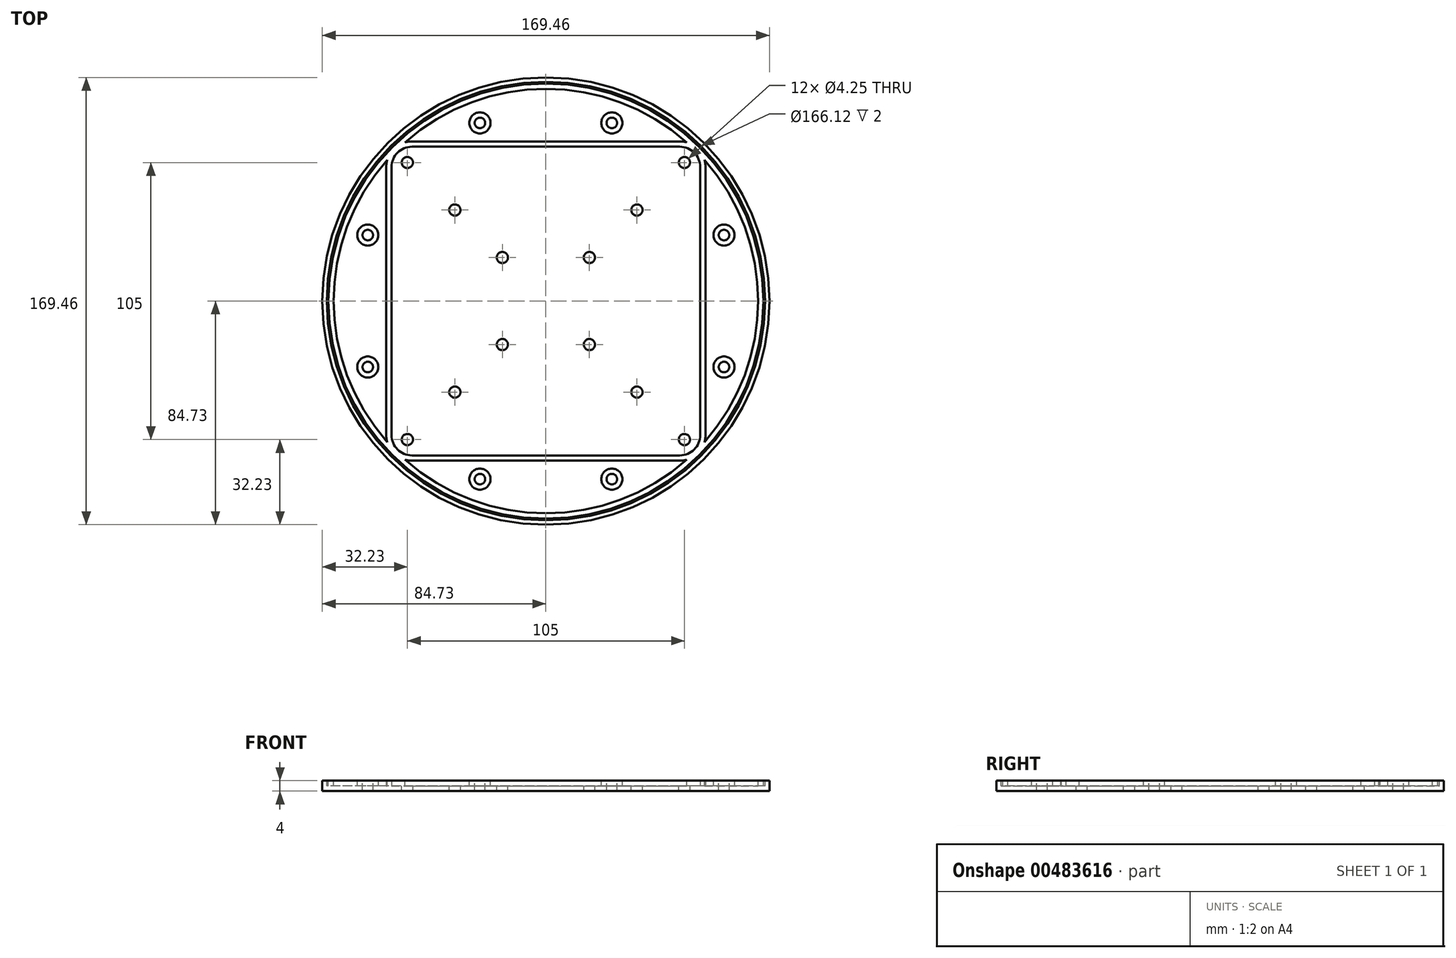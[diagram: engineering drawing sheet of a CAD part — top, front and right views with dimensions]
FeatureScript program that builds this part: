
annotation { "Feature Type Name" : "Feature", "Feature Type Description" : "" }
export const myFeature = defineFeature(function(context is Context, id is Id, definition is map)
    precondition{}
    {
        {
            var Q0;
            Q0=qCreatedBy(makeId("Top.planeOp"),FACE);
            var sketch = newSketch(context, id + "F0", { "sketchPlane" : qUnion([Q0])});
            skLineSegment(sketch, "E0.bottom", {"start": v(50.75, 58.5) * mm, "end": v(-50.75, 58.5) * mm});
            skLineSegment(sketch, "E0.top", {"start": v(50.75, -58.5) * mm, "end": v(-50.75, -58.5) * mm});
            skLineSegment(sketch, "E0.left", {"start": v(58.5, 50.75) * mm, "end": v(58.5, -50.75) * mm});
            skLineSegment(sketch, "E0.right", {"start": v(-58.5, 50.75) * mm, "end": v(-58.5, -50.75) * mm});
            skPoint(sketch, "E0.middle", {"position": v(0, 0) * mm});
            skCircle(sketch, "E1", {"center": v(0, 0) * mm, "radius": 82.73 * mm});
            skCircle(sketch, "E2", {"center": v(0, 0) * mm, "radius": 84.73 * mm});
            skLineSegment(sketch, "E3.bottom", {"start": v(48.75, 56.5) * mm, "end": v(-48.75, 56.5) * mm});
            skLineSegment(sketch, "E3.top", {"start": v(48.75, -56.5) * mm, "end": v(-48.75, -56.5) * mm});
            skLineSegment(sketch, "E3.left", {"start": v(56.5, 48.75) * mm, "end": v(56.5, -48.75) * mm});
            skLineSegment(sketch, "E3.right", {"start": v(-56.5, 48.75) * mm, "end": v(-56.5, -48.75) * mm});
            skLineSegment(sketch, "E4", {"start": v(-24, 58.5) * mm, "end": v(-24, 56.5) * mm});
            skLineSegment(sketch, "E5.MirrorCS", {"start": v(24, 58.5) * mm, "end": v(24, 56.5) * mm});
            skLineSegment(sketch, "E6.1.0", {"start": v(-58.5, -24) * mm, "end": v(-56.5, -24) * mm});
            skLineSegment(sketch, "E6.1.1", {"start": v(-58.5, 24) * mm, "end": v(-56.5, 24) * mm});
            skLineSegment(sketch, "E6.2.0", {"start": v(24, -58.5) * mm, "end": v(24, -56.5) * mm});
            skLineSegment(sketch, "E6.2.1", {"start": v(-24, -58.5) * mm, "end": v(-24, -56.5) * mm});
            skLineSegment(sketch, "E6.3.0", {"start": v(58.5, 24) * mm, "end": v(56.5, 24) * mm});
            skLineSegment(sketch, "E6.3.1", {"start": v(58.5, -24) * mm, "end": v(56.5, -24) * mm});
            skPoint(sketch, "E7.visualSharp", {"position": v(-58.5, 58.5) * mm});
            skArc(sketch, "E7.filletArc", {"start": v(-50.75, 58.5) * mm, "mid": v(-56.23, 56.23) * mm, "end": v(-58.5, 50.75) * mm});
            skPoint(sketch, "E8.visualSharp", {"position": v(-56.5, 56.5) * mm});
            skArc(sketch, "E8.filletArc", {"start": v(-48.75, 56.5) * mm, "mid": v(-54.23, 54.23) * mm, "end": v(-56.5, 48.75) * mm});
            skPoint(sketch, "E9.visualSharp", {"position": v(56.5, 56.5) * mm});
            skArc(sketch, "E9.filletArc", {"start": v(56.5, 48.75) * mm, "mid": v(54.23, 54.23) * mm, "end": v(48.75, 56.5) * mm});
            skPoint(sketch, "E10.visualSharp", {"position": v(58.5, 58.5) * mm});
            skArc(sketch, "E10.filletArc", {"start": v(58.5, 50.75) * mm, "mid": v(56.23, 56.23) * mm, "end": v(50.75, 58.5) * mm});
            skPoint(sketch, "E11.visualSharp", {"position": v(56.5, -56.5) * mm});
            skArc(sketch, "E11.filletArc", {"start": v(48.75, -56.5) * mm, "mid": v(54.23, -54.23) * mm, "end": v(56.5, -48.75) * mm});
            skPoint(sketch, "E12.visualSharp", {"position": v(58.5, -58.5) * mm});
            skArc(sketch, "E12.filletArc", {"start": v(50.75, -58.5) * mm, "mid": v(56.23, -56.23) * mm, "end": v(58.5, -50.75) * mm});
            skPoint(sketch, "E13.visualSharp", {"position": v(-58.5, -58.5) * mm});
            skArc(sketch, "E13.filletArc", {"start": v(-58.5, -50.75) * mm, "mid": v(-56.23, -56.23) * mm, "end": v(-50.75, -58.5) * mm});
            skPoint(sketch, "E14.visualSharp", {"position": v(-56.5, -56.5) * mm});
            skArc(sketch, "E14.filletArc", {"start": v(-56.5, -48.75) * mm, "mid": v(-54.23, -54.23) * mm, "end": v(-48.75, -56.5) * mm});
            skSolve(sketch);
        }
        {
            var Q0;
            {var subQ3=sQuery(id+"F0.wireOp",EDGE,"E6.1.0");Q0=makeQuery(id+"F0.imprint","IMPRINT",FACE,{"disambiguationData":[TD([[makeQuery(id+"F0.imprint","IMPRINT",EDGE,{"derivedFrom":subQ3}),-1.0]])]});}
            var Q1;
            {var subQ7=sQuery(id+"F0.wireOp",EDGE,"E6.2.0");Q1=makeQuery(id+"F0.imprint","IMPRINT",FACE,{"disambiguationData":[TD([[makeQuery(id+"F0.imprint","IMPRINT",EDGE,{"derivedFrom":subQ7}),-1.0]])]});}
            var Q2;
            {var subQ4=sQuery(id+"F0.wireOp",EDGE,"E5.MirrorCS");Q2=makeQuery(id+"F0.imprint","IMPRINT",FACE,{"disambiguationData":[TD([[makeQuery(id+"F0.imprint","IMPRINT",EDGE,{"derivedFrom":subQ4}),1.0]])]});}
            var Q3;
            {var subQ4=sQuery(id+"F0.wireOp",EDGE,"E4");Q3=makeQuery(id+"F0.imprint","IMPRINT",FACE,{"disambiguationData":[TD([[makeQuery(id+"F0.imprint","IMPRINT",EDGE,{"derivedFrom":subQ4}),-1.0]])]});}
            var Q4;
            {var subQ1=sQuery(id+"F0.wireOp",EDGE,"E0.top");var subQ3=makeQuery(id+"F0.imprint","INTERSECT",VERTEX,{"derivedFrom":[subQ1,sQuery(id+"F0.wireOp",EDGE,"E6.2.0")]});Q4=makeQuery(id+"F0.imprint","IMPRINT",FACE,{"disambiguationData":[TD([[makeQuery(id+"F0.imprint","IMPRINT",EDGE,{"disambiguationData":[TD([[subQ3,-1.0]])],"derivedFrom":subQ1}),1.0]])]});}
            var Q5;
            {var subQ1=sQuery(id+"F0.wireOp",EDGE,"E0.right");var subQ4=makeQuery(id+"F0.imprint","INTERSECT",VERTEX,{"derivedFrom":[subQ1,sQuery(id+"F0.wireOp",EDGE,"E6.1.0")]});Q5=makeQuery(id+"F0.imprint","IMPRINT",FACE,{"disambiguationData":[TD([[makeQuery(id+"F0.imprint","IMPRINT",EDGE,{"disambiguationData":[TD([[subQ4,1.0]])],"derivedFrom":subQ1}),-1.0]])]});}
            var Q6;
            {var subQ1=sQuery(id+"F0.wireOp",EDGE,"E0.bottom");var subQ4=makeQuery(id+"F0.imprint","INTERSECT",VERTEX,{"derivedFrom":[subQ1,sQuery(id+"F0.wireOp",EDGE,"E4")]});Q6=makeQuery(id+"F0.imprint","IMPRINT",FACE,{"disambiguationData":[TD([[makeQuery(id+"F0.imprint","IMPRINT",EDGE,{"disambiguationData":[TD([[subQ4,1.0]])],"derivedFrom":subQ1}),-1.0]])]});}
            var Q7;
            {var subQ1=sQuery(id+"F0.wireOp",EDGE,"E0.left");var subQ3=makeQuery(id+"F0.imprint","INTERSECT",VERTEX,{"derivedFrom":[subQ1,sQuery(id+"F0.wireOp",EDGE,"E6.3.0")]});Q7=makeQuery(id+"F0.imprint","IMPRINT",FACE,{"disambiguationData":[TD([[makeQuery(id+"F0.imprint","IMPRINT",EDGE,{"disambiguationData":[TD([[subQ3,-1.0]])],"derivedFrom":subQ1}),1.0]])]});}
            var Q8;
            Q8=makeQuery(id+"F0.imprint","IMPRINT",FACE,{"disambiguationData":[TD([[makeQuery(id+"F0.imprint","IMPRINT",EDGE,{"derivedFrom":sQuery(id+"F0.wireOp",EDGE,"E2")}),1.0]])]});
            var Q9;
            {var subQ1=sQuery(id+"F0.wireOp",EDGE,"E3.bottom");var subQ4=sQuery(id+"F0.wireOp",EDGE,"E3.left");var subQ9=makeQuery(id+"F0.imprint","INTERSECT",VERTEX,{"derivedFrom":[subQ1,subQ4]});Q9=makeQuery(id+"F0.imprint","IMPRINT",FACE,{"disambiguationData":[TD([[makeQuery(id+"F0.imprint","IMPRINT",EDGE,{"disambiguationData":[TD([[subQ9,-1.0]])],"derivedFrom":subQ1}),1.0]])]});}
            var Q10;
            {var subQ0=sQuery(id+"F0.wireOp",EDGE,"E6.1.0");Q10=makeQuery(id+"F0.imprint","IMPRINT",FACE,{"disambiguationData":[TD([[makeQuery(id+"F0.imprint","IMPRINT",EDGE,{"derivedFrom":subQ0}),1.0]])]});}
            var Q11;
            {var subQ0=sQuery(id+"F0.wireOp",EDGE,"E4");Q11=makeQuery(id+"F0.imprint","IMPRINT",FACE,{"disambiguationData":[TD([[makeQuery(id+"F0.imprint","IMPRINT",EDGE,{"derivedFrom":subQ0}),1.0]])]});}
            var Q12;
            {var subQ0=sQuery(id+"F0.wireOp",EDGE,"E6.2.0");Q12=makeQuery(id+"F0.imprint","IMPRINT",FACE,{"disambiguationData":[TD([[makeQuery(id+"F0.imprint","IMPRINT",EDGE,{"derivedFrom":subQ0}),1.0]])]});}
            var Q13;
            {var subQ0=sQuery(id+"F0.wireOp",EDGE,"E6.3.0");Q13=makeQuery(id+"F0.imprint","IMPRINT",FACE,{"disambiguationData":[TD([[makeQuery(id+"F0.imprint","IMPRINT",EDGE,{"derivedFrom":subQ0}),1.0]])]});}
            extrude(context, id + "F1", {"entities" : qUnion([Q0, Q1, Q2, Q3, Q4, Q5, Q6, Q7, Q8, Q9, Q10, Q11, Q12, Q13]), "depth" : 2 * mm});
        }
        {
            var Q0;
            {var subQ1=sQuery(id+"F0.wireOp",EDGE,"E0.top");var subQ3=makeQuery(id+"F0.imprint","INTERSECT",VERTEX,{"derivedFrom":[subQ1,sQuery(id+"F0.wireOp",EDGE,"E6.2.0")]});Q0=makeQuery(id+"F0.imprint","IMPRINT",FACE,{"disambiguationData":[TD([[makeQuery(id+"F0.imprint","IMPRINT",EDGE,{"disambiguationData":[TD([[subQ3,-1.0]])],"derivedFrom":subQ1}),1.0]])]});}
            var Q1;
            {var subQ1=sQuery(id+"F0.wireOp",EDGE,"E0.right");var subQ4=makeQuery(id+"F0.imprint","INTERSECT",VERTEX,{"derivedFrom":[subQ1,sQuery(id+"F0.wireOp",EDGE,"E6.1.0")]});Q1=makeQuery(id+"F0.imprint","IMPRINT",FACE,{"disambiguationData":[TD([[makeQuery(id+"F0.imprint","IMPRINT",EDGE,{"disambiguationData":[TD([[subQ4,1.0]])],"derivedFrom":subQ1}),-1.0]])]});}
            var Q2;
            Q2=makeQuery(id+"F0.imprint","IMPRINT",FACE,{"disambiguationData":[TD([[makeQuery(id+"F0.imprint","IMPRINT",EDGE,{"derivedFrom":sQuery(id+"F0.wireOp",EDGE,"E2")}),1.0]])]});
            var Q3;
            {var subQ1=sQuery(id+"F0.wireOp",EDGE,"E0.bottom");var subQ4=makeQuery(id+"F0.imprint","INTERSECT",VERTEX,{"derivedFrom":[subQ1,sQuery(id+"F0.wireOp",EDGE,"E4")]});Q3=makeQuery(id+"F0.imprint","IMPRINT",FACE,{"disambiguationData":[TD([[makeQuery(id+"F0.imprint","IMPRINT",EDGE,{"disambiguationData":[TD([[subQ4,1.0]])],"derivedFrom":subQ1}),-1.0]])]});}
            var Q4;
            {var subQ1=sQuery(id+"F0.wireOp",EDGE,"E0.left");var subQ3=makeQuery(id+"F0.imprint","INTERSECT",VERTEX,{"derivedFrom":[subQ1,sQuery(id+"F0.wireOp",EDGE,"E6.3.0")]});Q4=makeQuery(id+"F0.imprint","IMPRINT",FACE,{"disambiguationData":[TD([[makeQuery(id+"F0.imprint","IMPRINT",EDGE,{"disambiguationData":[TD([[subQ3,-1.0]])],"derivedFrom":subQ1}),1.0]])]});}
            extrude(context, id + "F2", {"entities" : qUnion([Q0, Q1, Q2, Q3, Q4]), "operationType" : NewBodyOperationType.ADD, "depth" : 4 * mm});
        }
        {
            var Q0;
            Q0=makeQuery(id+"F2.opExtrude","CAP_FACE",FACE,{"disambiguationData":[OSD([sQuery(id+"F0.wireOp",EDGE,"E0.bottom"),sQuery(id+"F0.wireOp",EDGE,"E0.top"),sQuery(id+"F0.wireOp",EDGE,"E0.left"),sQuery(id+"F0.wireOp",EDGE,"E0.right"),sQuery(id+"F0.wireOp",EDGE,"E2")])],"isStart":false});
            var sketch = newSketch(context, id + "F3", { "sketchPlane" : qUnion([Q0])});
            skCircle(sketch, "E15", {"center": v(0, 0) * mm, "radius": 82.44 * mm});
            skCircle(sketch, "E16", {"center": v(0, 0) * mm, "radius": 83.06 * mm});
            skSolve(sketch);
        }
        {
            var Q0;
            Q0=makeQuery(id+"F3.imprint","IMPRINT",FACE,{"disambiguationData":[TD([[makeQuery(id+"F3.imprint","IMPRINT",EDGE,{"derivedFrom":sQuery(id+"F3.wireOp",EDGE,"E15")}),-1.0]])]});
            extrude(context, id + "F4", {"entities" : qUnion([Q0]), "operationType" : NewBodyOperationType.REMOVE, "oppositeDirection" : true, "depth" : 2 * mm});
        }
        {
            var Q0;
            Q0=makeQuery(id+"F1.opExtrude","CAP_FACE",FACE,{"disambiguationData":[OSD([sQuery(id+"F0.wireOp",EDGE,"E2")])],"isStart":false});
            var sketch = newSketch(context, id + "F5", { "sketchPlane" : qUnion([Q0])});
            skPoint(sketch, "E17.middle", {"position": v(0, 0) * mm});
            skLineSegment(sketch, "E18.bottom", {"start": v(58.5, 58.5) * mm, "end": v(-58.5, 58.5) * mm});
            skLineSegment(sketch, "E18.top", {"start": v(58.5, -58.5) * mm, "end": v(-58.5, -58.5) * mm});
            skLineSegment(sketch, "E18.left", {"start": v(58.5, 58.5) * mm, "end": v(58.5, -58.5) * mm});
            skLineSegment(sketch, "E18.right", {"start": v(-58.5, 58.5) * mm, "end": v(-58.5, -58.5) * mm});
            skCircle(sketch, "E19", {"center": v(-52.5, 52.5) * mm, "radius": 2.12 * mm});
            skCircle(sketch, "E20.1.0", {"center": v(-52.5, -52.5) * mm, "radius": 2.12 * mm});
            skCircle(sketch, "E20.2.0", {"center": v(52.5, -52.5) * mm, "radius": 2.12 * mm});
            skCircle(sketch, "E20.3.0", {"center": v(52.5, 52.5) * mm, "radius": 2.12 * mm});
            skCircle(sketch, "E21", {"center": v(-16.5, 16.5) * mm, "radius": 2.12 * mm});
            skCircle(sketch, "E22.1.0", {"center": v(-16.5, -16.5) * mm, "radius": 2.12 * mm});
            skCircle(sketch, "E22.2.0", {"center": v(16.5, -16.5) * mm, "radius": 2.12 * mm});
            skCircle(sketch, "E22.3.0", {"center": v(16.5, 16.5) * mm, "radius": 2.12 * mm});
            skCircle(sketch, "E23", {"center": v(34.5, -34.5) * mm, "radius": 2.12 * mm});
            skCircle(sketch, "E24.1.0", {"center": v(34.5, 34.5) * mm, "radius": 2.12 * mm});
            skCircle(sketch, "E24.2.0", {"center": v(-34.5, 34.5) * mm, "radius": 2.12 * mm});
            skCircle(sketch, "E24.3.0", {"center": v(-34.5, -34.5) * mm, "radius": 2.12 * mm});
            skSolve(sketch);
        }
        {
            var Q0;
            Q0=makeQuery(id+"F5.imprint","IMPRINT",FACE,{"disambiguationData":[TD([[makeQuery(id+"F5.imprint","IMPRINT",EDGE,{"derivedFrom":sQuery(id+"F5.wireOp",EDGE,"E19")}),1.0]])]});
            var Q1;
            Q1=makeQuery(id+"F5.imprint","IMPRINT",FACE,{"disambiguationData":[TD([[makeQuery(id+"F5.imprint","IMPRINT",EDGE,{"derivedFrom":sQuery(id+"F5.wireOp",EDGE,"E20.3.0")}),1.0]])]});
            var Q2;
            Q2=makeQuery(id+"F5.imprint","IMPRINT",FACE,{"disambiguationData":[TD([[makeQuery(id+"F5.imprint","IMPRINT",EDGE,{"derivedFrom":sQuery(id+"F5.wireOp",EDGE,"E20.1.0")}),1.0]])]});
            var Q3;
            Q3=makeQuery(id+"F5.imprint","IMPRINT",FACE,{"disambiguationData":[TD([[makeQuery(id+"F5.imprint","IMPRINT",EDGE,{"derivedFrom":sQuery(id+"F5.wireOp",EDGE,"E20.2.0")}),1.0]])]});
            var Q4;
            Q4=makeQuery(id+"F5.imprint","IMPRINT",FACE,{"disambiguationData":[TD([[makeQuery(id+"F5.imprint","IMPRINT",EDGE,{"derivedFrom":sQuery(id+"F5.wireOp",EDGE,"E22.3.0")}),1.0]])]});
            var Q5;
            Q5=makeQuery(id+"F5.imprint","IMPRINT",FACE,{"disambiguationData":[TD([[makeQuery(id+"F5.imprint","IMPRINT",EDGE,{"derivedFrom":sQuery(id+"F5.wireOp",EDGE,"E21")}),1.0]])]});
            var Q6;
            Q6=makeQuery(id+"F5.imprint","IMPRINT",FACE,{"disambiguationData":[TD([[makeQuery(id+"F5.imprint","IMPRINT",EDGE,{"derivedFrom":sQuery(id+"F5.wireOp",EDGE,"E22.1.0")}),1.0]])]});
            var Q7;
            Q7=makeQuery(id+"F5.imprint","IMPRINT",FACE,{"disambiguationData":[TD([[makeQuery(id+"F5.imprint","IMPRINT",EDGE,{"derivedFrom":sQuery(id+"F5.wireOp",EDGE,"E22.2.0")}),1.0]])]});
            var Q8;
            Q8=makeQuery(id+"F5.imprint","IMPRINT",FACE,{"disambiguationData":[TD([[makeQuery(id+"F5.imprint","IMPRINT",EDGE,{"derivedFrom":sQuery(id+"F5.wireOp",EDGE,"E24.2.0")}),1.0]])]});
            var Q9;
            Q9=makeQuery(id+"F5.imprint","IMPRINT",FACE,{"disambiguationData":[TD([[makeQuery(id+"F5.imprint","IMPRINT",EDGE,{"derivedFrom":sQuery(id+"F5.wireOp",EDGE,"E24.1.0")}),1.0]])]});
            var Q10;
            Q10=makeQuery(id+"F5.imprint","IMPRINT",FACE,{"disambiguationData":[TD([[makeQuery(id+"F5.imprint","IMPRINT",EDGE,{"derivedFrom":sQuery(id+"F5.wireOp",EDGE,"E23")}),1.0]])]});
            var Q11;
            Q11=makeQuery(id+"F5.imprint","IMPRINT",FACE,{"disambiguationData":[TD([[makeQuery(id+"F5.imprint","IMPRINT",EDGE,{"derivedFrom":sQuery(id+"F5.wireOp",EDGE,"E24.3.0")}),1.0]])]});
            extrude(context, id + "F6", {"entities" : qUnion([Q0, Q1, Q2, Q3, Q4, Q5, Q6, Q7, Q8, Q9, Q10, Q11]), "operationType" : NewBodyOperationType.REMOVE, "oppositeDirection" : true, "depth" : 25 * mm});
        }
        {
            var Q0;
            Q0=makeQuery(id+"F1.opExtrude","CAP_FACE",FACE,{"disambiguationData":[OSD([sQuery(id+"F0.wireOp",EDGE,"E2")])],"isStart":false});
            var sketch = newSketch(context, id + "F7", { "sketchPlane" : qUnion([Q0])});
            skCircle(sketch, "E25", {"center": v(0, -8) * mm, "radius": 14.5 * mm});
            skCircle(sketch, "E26", {"center": v(-17.5, -8) * mm, "radius": 1.5 * mm});
            skCircle(sketch, "E27.1.0", {"center": v(17.5, -8) * mm, "radius": 1.5 * mm});
            skCircle(sketch, "E28", {"center": v(-17.5, -8) * mm, "radius": 3 * mm});
            skCircle(sketch, "E29.1.0", {"center": v(17.5, -8) * mm, "radius": 3 * mm});
            skSolve(sketch);
        }
        {
            var Q0;
            {var subQ0=sQuery(id+"F0.wireOp",EDGE,"E0.left");var subQ1=sQuery(id+"F0.wireOp",EDGE,"E0.top");var subQ2=sQuery(id+"F0.wireOp",EDGE,"E0.right");var subQ3=sQuery(id+"F0.wireOp",EDGE,"E0.bottom");var subQ4=sQuery(id+"F0.wireOp",EDGE,"E7.filletArc");var subQ5=sQuery(id+"F0.wireOp",EDGE,"E10.filletArc");var subQ6=sQuery(id+"F0.wireOp",EDGE,"E12.filletArc");var subQ7=sQuery(id+"F0.wireOp",EDGE,"E13.filletArc");Q0=makeQuery(id+"F4.boolean.opBoolean","SPLIT",FACE,{"disambiguationData":[TD([makeQuery(id+"F2.opExtrude","SWEPT_FACE",FACE,{"disambiguationData":[OSD([subQ3])]})])],"derivedFrom":makeQuery(id+"F2.opExtrude","CAP_FACE",FACE,{"disambiguationData":[OSD([subQ3,subQ1,subQ0,subQ2,sQuery(id+"F0.wireOp",EDGE,"E2"),subQ4,subQ5,subQ6,subQ7])],"isStart":false})});}
            var sketch = newSketch(context, id + "F8", { "sketchPlane" : qUnion([Q0])});
            skLineSegment(sketch, "E30.bottom", {"start": v(25, 67.5) * mm, "end": v(-25, 67.5) * mm});
            skLineSegment(sketch, "E30.top", {"start": v(25, -67.5) * mm, "end": v(-25, -67.5) * mm});
            skLineSegment(sketch, "E30.left", {"start": v(25, 67.5) * mm, "end": v(25, -67.5) * mm});
            skLineSegment(sketch, "E30.right", {"start": v(-25, 67.5) * mm, "end": v(-25, -67.5) * mm});
            skPoint(sketch, "E30.middle", {"position": v(0, 0) * mm});
            skLineSegment(sketch, "E31.bottom", {"start": v(67.5, 25) * mm, "end": v(-67.5, 25) * mm});
            skLineSegment(sketch, "E31.top", {"start": v(67.5, -25) * mm, "end": v(-67.5, -25) * mm});
            skLineSegment(sketch, "E31.left", {"start": v(67.5, 25) * mm, "end": v(67.5, -25) * mm});
            skLineSegment(sketch, "E31.right", {"start": v(-67.5, 25) * mm, "end": v(-67.5, -25) * mm});
            skSolve(sketch);
        }
        {
            var Q0;
            Q0=sQuery(id+"F8.wireOp",VERTEX,"E30.right.start");
            var Q1;
            Q1=sQuery(id+"F8.wireOp",VERTEX,"E30.left.start");
            var Q2;
            Q2=sQuery(id+"F8.wireOp",VERTEX,"E31.left.start");
            var Q3;
            Q3=sQuery(id+"F8.wireOp",VERTEX,"E31.top.start");
            var Q4;
            Q4=sQuery(id+"F8.wireOp",VERTEX,"E30.left.end");
            var Q5;
            Q5=sQuery(id+"F8.wireOp",VERTEX,"E31.bottom.end");
            var Q6;
            Q6=sQuery(id+"F8.wireOp",VERTEX,"E30.right.end");
            var Q7;
            Q7=sQuery(id+"F8.wireOp",VERTEX,"E31.top.end");
            var Q8;
            Q8=makeQuery(id+"F1.opExtrude","SWEPT_BODY",BODY,{"disambiguationData":[OSD([sQuery(id+"F0.wireOp",EDGE,"E2")])]});
            hole(context, id + "F9", {"style" : HoleStyle.SIMPLE, "endStyle" : HoleEndStyle.BLIND, "holeDiameter" : 4 * mm, "holeDepth" : 12 * mm, "isTappedThrough" : true, "tappedDepth" : 12 * mm, "tapClearance" : 3, "locations" : qUnion([Q0, Q1, Q2, Q3, Q4, Q5, Q6, Q7]), "scope" : qUnion([Q8])});
        }
        {
            var Q0;
            {var subQ0=sQuery(id+"F0.wireOp",EDGE,"E0.left");var subQ1=sQuery(id+"F0.wireOp",EDGE,"E0.top");var subQ2=sQuery(id+"F0.wireOp",EDGE,"E0.right");var subQ3=sQuery(id+"F0.wireOp",EDGE,"E0.bottom");var subQ4=sQuery(id+"F0.wireOp",EDGE,"E7.filletArc");var subQ5=sQuery(id+"F0.wireOp",EDGE,"E10.filletArc");var subQ6=sQuery(id+"F0.wireOp",EDGE,"E12.filletArc");var subQ7=sQuery(id+"F0.wireOp",EDGE,"E13.filletArc");Q0=makeQuery(id+"F4.boolean.opBoolean","SPLIT",FACE,{"disambiguationData":[TD([makeQuery(id+"F2.opExtrude","SWEPT_FACE",FACE,{"disambiguationData":[OSD([subQ3])]})])],"derivedFrom":makeQuery(id+"F2.opExtrude","CAP_FACE",FACE,{"disambiguationData":[OSD([subQ3,subQ1,subQ0,subQ2,sQuery(id+"F0.wireOp",EDGE,"E2"),subQ4,subQ5,subQ6,subQ7])],"isStart":false})});}
            shell(context, id + "F10", {"entities" : qUnion([Q0]), "thickness" : 2 * mm});
        }
    });
